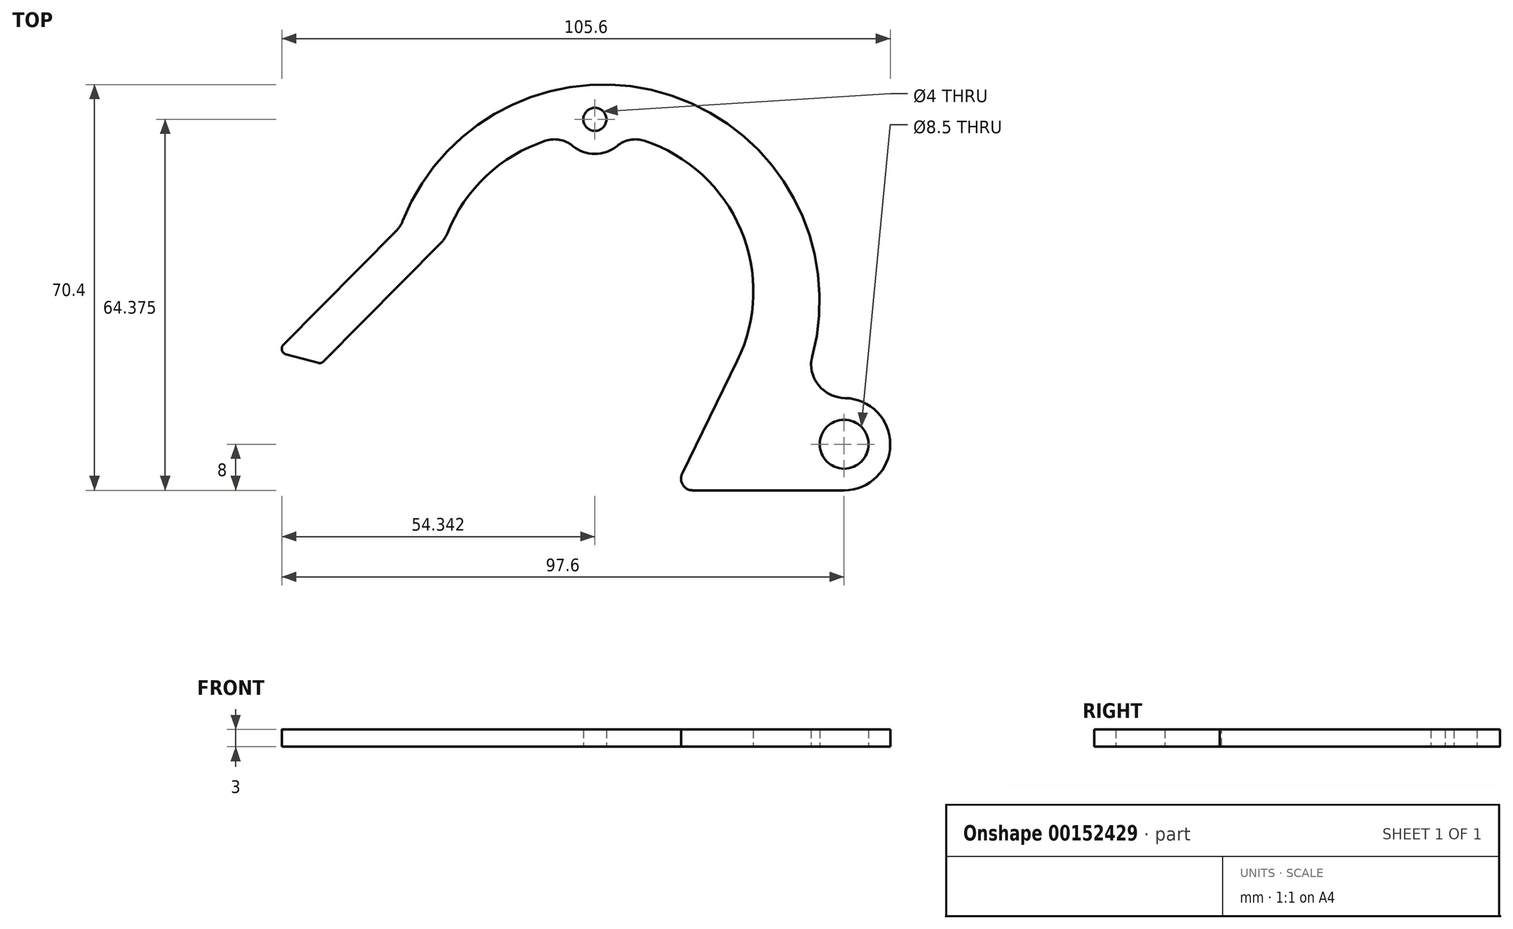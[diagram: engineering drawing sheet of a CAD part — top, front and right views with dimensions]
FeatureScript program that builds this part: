
annotation { "Feature Type Name" : "Feature", "Feature Type Description" : "" }
export const myFeature = defineFeature(function(context is Context, id is Id, definition is map)
    precondition{}
    {
        {
            var Q0;
            Q0=qCreatedBy(makeId("Top.planeOp"),FACE);
            var sketch = newSketch(context, id + "F0", { "sketchPlane" : qUnion([Q0])});
            skLineSegment(sketch, "E0", {"start": v(3.2, 0) * mm, "end": v(29.5, 0) * mm});
            skArc(sketch, "E1", {"start": v(29.5, 0) * mm, "mid": v(37.5, 8) * mm, "end": v(29.5, 16) * mm});
            skCircle(sketch, "E2", {"center": v(29.5, 8) * mm, "radius": 4.25 * mm});
            skLineSegment(sketch, "E3", {"start": v(29.5, 8) * mm, "end": v(29.5, 16) * mm, "construction": true});
            skLineSegment(sketch, "E4", {"start": v(1.4, 2.88) * mm, "end": v(10.96, 22.47) * mm});
            skPoint(sketch, "E5.visualSharp", {"position": v(0, 0) * mm});
            skArc(sketch, "E5.filletArc", {"start": v(1.4, 2.88) * mm, "mid": v(1.5, 0.94) * mm, "end": v(3.2, 0) * mm});
            skLineSegment(sketch, "E6", {"start": v(1.4, 2.88) * mm, "end": v(0, 0) * mm, "construction": true});
            skPoint(sketch, "E7", {"position": v(10.96, 22.47) * mm});
            skPoint(sketch, "E8", {"position": v(37.5, 8) * mm});
            skCircle(sketch, "E9", {"center": v(-13.76, 34.53) * mm, "radius": 27.5 * mm});
            skCircle(sketch, "E10", {"center": v(-12.25, 32.9) * mm, "radius": 37.5 * mm});
            skLineSegment(sketch, "E11", {"start": v(23.75, 16) * mm, "end": v(23.75, 22.4) * mm});
            skPoint(sketch, "E12", {"position": v(25.25, 8) * mm});
            skLineSegment(sketch, "E13", {"start": v(25.25, 15.56) * mm, "end": v(25.25, 16) * mm, "construction": true});
            skLineSegment(sketch, "E14", {"start": v(0, 0) * mm, "end": v(-47.45, 45.83) * mm, "construction": true});
            skPoint(sketch, "E15", {"position": v(-47.45, 45.83) * mm});
            skLineSegment(sketch, "E16", {"start": v(-47.45, 45.83) * mm, "end": v(-39.67, 43.74) * mm, "construction": true});
            skLineSegment(sketch, "E17", {"start": v(-39.67, 43.74) * mm, "end": v(-18.28, 43.74) * mm, "construction": true});
            skLineSegment(sketch, "E18", {"start": v(-39.67, 43.74) * mm, "end": v(-53.66, 43.74) * mm, "construction": true});
            skLineSegment(sketch, "E19", {"start": v(-47.45, 45.83) * mm, "end": v(-69.02, 24.05) * mm});
            skLineSegment(sketch, "E20", {"start": v(-69.02, 24.05) * mm, "end": v(-61.23, 21.96) * mm});
            skLineSegment(sketch, "E21", {"start": v(-39.67, 43.74) * mm, "end": v(-61.23, 21.96) * mm});
            skLineSegment(sketch, "E22", {"start": v(-13.76, 34.53) * mm, "end": v(-13.76, 70.37) * mm, "construction": true});
            skCircle(sketch, "E23", {"center": v(-13.76, 64.37) * mm, "radius": 6 * mm});
            skCircle(sketch, "E24", {"center": v(-13.76, 64.37) * mm, "radius": 2 * mm});
            skLineSegment(sketch, "E25", {"start": v(29.5, 16) * mm, "end": v(23.75, 16) * mm});
            skPoint(sketch, "E26.orphan", {"position": v(23.75, 15.4) * mm});
            skPoint(sketch, "E27.endSnap0", {"position": v(-5.81, -11.91) * mm});
            skPoint(sketch, "E28.orphan", {"position": v(-11.62, -23.83) * mm});
            skPoint(sketch, "E27.start.orphan", {"position": v(-30.24, 0) * mm});
            skPoint(sketch, "E29", {"position": v(21.45, 16.47) * mm});
            skLineSegment(sketch, "E30", {"start": v(10.6, 21.76) * mm, "end": v(10.61, 21.76) * mm, "construction": true});
            skPoint(sketch, "E31.end.orphan", {"position": v(32.88, 67.4) * mm});
            skLineSegment(sketch, "E32", {"start": v(23.75, 22.4) * mm, "end": v(23.75, 67.68) * mm, "construction": true});
            skLineSegment(sketch, "E33", {"start": v(-13.76, 34.53) * mm, "end": v(-12.25, 32.9) * mm});
            skSolve(sketch);
        }
        {
            var Q0;
            {var subQ0=sQuery(id+"F0.wireOp",EDGE,"E19");Q0=makeQuery(id+"F0.imprint","IMPRINT",FACE,{"disambiguationData":[TD([[makeQuery(id+"F0.imprint","IMPRINT",EDGE,{"derivedFrom":subQ0}),1.0]])]});}
            var Q1;
            {var subQ2=sQuery(id+"F0.wireOp",EDGE,"E21");var subQ6=sQuery(id+"F0.wireOp",EDGE,"E9");var subQ7=makeQuery(id+"F0.imprint","INTERSECT",VERTEX,{"derivedFrom":[subQ6,subQ2]});Q1=makeQuery(id+"F0.imprint","IMPRINT",FACE,{"disambiguationData":[TD([[makeQuery(id+"F0.imprint","IMPRINT",EDGE,{"disambiguationData":[TD([[subQ7,1.0]])],"derivedFrom":subQ6}),-1.0]])]});}
            var Q2;
            {var subQ0=sQuery(id+"F0.wireOp",EDGE,"E23");var subQ1=sQuery(id+"F0.wireOp",EDGE,"E9");var subQ2=makeQuery(id+"F0.imprint","INTERSECT",VERTEX,{"disambiguationData":[OD(0.0)],"derivedFrom":[subQ1,subQ0]});Q2=makeQuery(id+"F0.imprint","IMPRINT",FACE,{"disambiguationData":[TD([[makeQuery(id+"F0.imprint","IMPRINT",EDGE,{"disambiguationData":[TD([[subQ2,1.0]])],"derivedFrom":subQ1}),-1.0]])]});}
            var Q3;
            {var subQ0=sQuery(id+"F0.wireOp",EDGE,"E23");var subQ1=sQuery(id+"F0.wireOp",EDGE,"E9");var subQ2=makeQuery(id+"F0.imprint","INTERSECT",VERTEX,{"disambiguationData":[OD(0.0)],"derivedFrom":[subQ1,subQ0]});Q3=makeQuery(id+"F0.imprint","IMPRINT",FACE,{"disambiguationData":[TD([[makeQuery(id+"F0.imprint","IMPRINT",EDGE,{"disambiguationData":[TD([[subQ2,1.0]])],"derivedFrom":subQ1}),1.0]])]});}
            var Q4;
            {var subQ1=sQuery(id+"F0.wireOp",EDGE,"E4");Q4=makeQuery(id+"F0.imprint","IMPRINT",FACE,{"disambiguationData":[TD([[makeQuery(id+"F0.imprint","IMPRINT",EDGE,{"derivedFrom":subQ1}),-1.0]])]});}
            var Q5;
            {var subQ4=sQuery(id+"F0.wireOp",EDGE,"E1");Q5=makeQuery(id+"F0.imprint","IMPRINT",FACE,{"disambiguationData":[TD([[makeQuery(id+"F0.imprint","IMPRINT",EDGE,{"derivedFrom":subQ4}),1.0]])]});}
            extrude(context, id + "F1", {"entities" : qUnion([Q0, Q1, Q2, Q3, Q4, Q5]), "depth" : 3 * mm});
        }
        {
            var Q0;
            {var subQ0=sQuery(id+"F0.wireOp",EDGE,"E23");var subQ1=sQuery(id+"F0.wireOp",EDGE,"E9");Q0=makeQuery(id+"F1.opExtrude","SWEPT_EDGE",EDGE,{"disambiguationData":[OSD([subQ1,subQ0]),TDD([makeQuery(id+"F0.imprint","INTERSECT",VERTEX,{"disambiguationData":[OD(0.0)],"derivedFrom":[subQ1,subQ0]})])]});}
            var Q1;
            {var subQ0=sQuery(id+"F0.wireOp",EDGE,"E23");var subQ1=sQuery(id+"F0.wireOp",EDGE,"E9");Q1=makeQuery(id+"F1.opExtrude","SWEPT_EDGE",EDGE,{"disambiguationData":[OSD([subQ1,subQ0]),TDD([makeQuery(id+"F0.imprint","INTERSECT",VERTEX,{"disambiguationData":[OD(1.0)],"derivedFrom":[subQ1,subQ0]})])]});}
            var Q2;
            Q2=makeQuery(id+"F1.opExtrude","SWEPT_EDGE",EDGE,{"disambiguationData":[OSD([sQuery(id+"F0.wireOp",EDGE,"E9"),sQuery(id+"F0.wireOp",EDGE,"E21")])]});
            var Q3;
            Q3=makeQuery(id+"F1.opExtrude","SWEPT_EDGE",EDGE,{"disambiguationData":[OSD([sQuery(id+"F0.wireOp",EDGE,"E10"),sQuery(id+"F0.wireOp",EDGE,"E19")])]});
            fillet(context, id + "F2", {"entities" : qUnion([Q0, Q1, Q2, Q3]), "radius" : 5 * mm, "tangentPropagation" : true, "allowEdgeOverflow" : false});
        }
        {
            var Q0;
            Q0=makeQuery(id+"F1.opExtrude","SWEPT_EDGE",EDGE,{"disambiguationData":[OSD([sQuery(id+"F0.wireOp",EDGE,"1qSlrM0i-sSkW-lbLZ-bidS-qWem4HMrsFkF"),sQuery(id+"F0.wireOp",EDGE,"E11")])]});
            var Q1;
            Q1=makeQuery(id+"F1.opExtrude","SWEPT_EDGE",EDGE,{"disambiguationData":[OSD([sQuery(id+"F0.wireOp",EDGE,"E10"),sQuery(id+"F0.wireOp",EDGE,"E11")])]});
            fillet(context, id + "F3", {"entities" : qUnion([Q0, Q1]), "radius" : 6 * mm, "tangentPropagation" : true, "allowEdgeOverflow" : false});
        }
        {
            var Q0;
            Q0=makeQuery(id+"F1.opExtrude","SWEPT_EDGE",EDGE,{"disambiguationData":[OSD([sQuery(id+"F0.wireOp",EDGE,"E19"),sQuery(id+"F0.wireOp",EDGE,"E20")])]});
            var Q1;
            Q1=makeQuery(id+"F1.opExtrude","SWEPT_EDGE",EDGE,{"disambiguationData":[OSD([sQuery(id+"F0.wireOp",EDGE,"E20"),sQuery(id+"F0.wireOp",EDGE,"E21")])]});
            fillet(context, id + "F4", {"entities" : qUnion([Q0, Q1]), "radius" : 1 * mm, "tangentPropagation" : true, "allowEdgeOverflow" : false});
        }
    });
